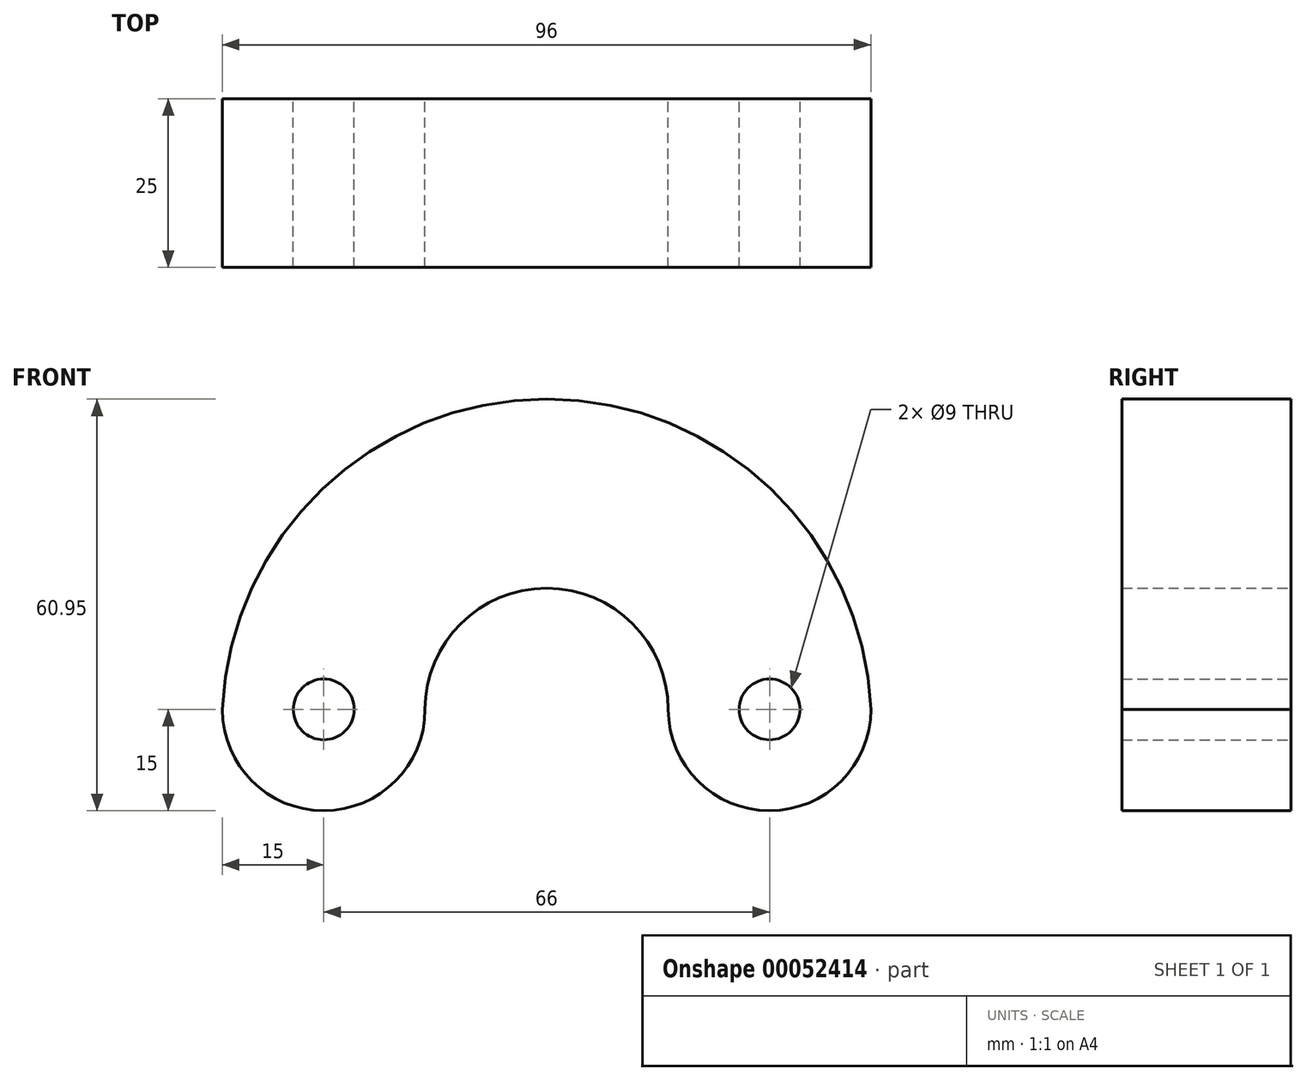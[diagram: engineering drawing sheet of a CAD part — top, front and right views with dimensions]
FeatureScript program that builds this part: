
annotation { "Feature Type Name" : "Feature", "Feature Type Description" : "" }
export const myFeature = defineFeature(function(context is Context, id is Id, definition is map)
    precondition{}
    {
        {
            var Q0;
            Q0=qCreatedBy(makeId("Front.planeOp"),FACE);
            var sketch = newSketch(context, id + "F0", { "sketchPlane" : qUnion([Q0])});
            skCircle(sketch, "E0", {"center": v(0, 0) * mm, "radius": 4.5 * mm});
            skCircle(sketch, "E1", {"center": v(66, 0) * mm, "radius": 4.5 * mm});
            skCircle(sketch, "E2", {"center": v(0, 0) * mm, "radius": 15 * mm});
            skCircle(sketch, "E3", {"center": v(66, 0) * mm, "radius": 15 * mm});
            skArc(sketch, "E4", {"start": v(51, 0) * mm, "mid": v(33, 17.95) * mm, "end": v(15, 0) * mm});
            skArc(sketch, "E5", {"start": v(81, 0) * mm, "mid": v(33, 45.95) * mm, "end": v(-15, 0) * mm});
            skSolve(sketch);
        }
        {
            var Q0;
            Q0=makeQuery(id+"F0.imprint","IMPRINT",FACE,{"disambiguationData":[TD([[makeQuery(id+"F0.imprint","IMPRINT",EDGE,{"derivedFrom":sQuery(id+"F0.wireOp",EDGE,"E1")}),-1.0]])]});
            var Q1;
            {var subQ0=sQuery(id+"F0.wireOp",EDGE,"E4");Q1=makeQuery(id+"F0.imprint","IMPRINT",FACE,{"disambiguationData":[TD([[makeQuery(id+"F0.imprint","IMPRINT",EDGE,{"derivedFrom":subQ0}),-1.0]])]});}
            var Q2;
            Q2=makeQuery(id+"F0.imprint","IMPRINT",FACE,{"disambiguationData":[TD([[makeQuery(id+"F0.imprint","IMPRINT",EDGE,{"derivedFrom":sQuery(id+"F0.wireOp",EDGE,"E0")}),-1.0]])]});
            extrude(context, id + "F1", {"entities" : qUnion([Q0, Q1, Q2]), "depth" : 25 * mm});
        }
    });
